# Revit family: Quantum_Odyssey_FBS2LED-DIF-xx_Non-Hosted_R16
name_source: partatom
category: Lighting Fixtures
revit_build: Autodesk Revit 2016 (Build: 20151007_0715(x64)
units: mm (PartAtom-declared; Revit-internal decimal feet)

## family parameters
Always vertical = Yes
Cut with Voids When Loaded = No
Light Source = Yes
OmniClass Number = 23.80.70.00
OmniClass Title = Lighting
Part Type = Normal
Room Calculation Point = No
Round Connector Dimension = Use Diameter
Shared = No
Work Plane-Based = No

## types (3) — shared parameters
Color Filter = 16777215
Construction = Powder Coated Steel Body and PC/ABS End Caps
Diffuser = Acrylic Prismatic Diffuser
Dimensions (L x W x H) = 630mm x 120mm x 108mm
Dimming Lamp Color Temperature Shift = <None>
Emit Shape Visible in Rendering = No
IP Rating = IP20
Lamp = LED Strip Module, 4,000K Natural White, 50,000h Life [L70/B50 Ta 40°C], Ra>80
Manufacturer = Clevertronics
Mounting = Surface mount
Operating Temperature = 1˚C to 40˚C
Operating Voltage = 240V AC; 50Hz
Photometric Web File = ll21966_FBS2LED-DIF_AUB04610050001.ies
Power Factor = 0.95
Replacement lamp = 8002695 PCA:LED Strip 8S6P, ALS-13-840-0-02-B
Tilt Angle = 90.00°
Weight = 1.8 kg

## per-type parameters (varying)
| type | Description | LED Driver | MIC Number | Power Consumption | Replacement Driver | Sensor | Total Lumen Output |
| FBS2LED-DIF-MS | Odyssey Quantum 240V 600mm LED diffused Batten with Microwave Motion Sensor Control (on/off) | Osram 40W, 500-1050mA, 15-50V | AUB04610070001 | 21 Watts | 1330029 LED Driver – 40w 500-1050 mA, 15-50V | 1190117 Sensor: Microwave motion, IP20, MC6025 | 2187 lm @ 104lm/W |
| FBS2LED-DIF | 240V Odyssey Quantum 600mm LED Diffused Batten | Osram 40W, 500-1050mA, 15-50V | AUB04610050001 | 20W | 1330029 LED Driver – 40w 500-1050 mA, 15-50V |  | 2200lm @ 105lm/W |
| FBS2LED-DIF-DD | 240V Odyssey Quantum LED Diffused Batten with DALI driver | LED DALI Driver 25w 350-1050mA, 20-50V, 50,000h | AUB04610060001 | 21 Watts | 1330038 LED Dali Driver – 25w 350-1050 mA, 20-50V |  | 2187lm @ 102lm/W |

note: column(s) folded — value = type name in every type: Model

## geometry (parser evidence)
native form markers: Sweep x3
no freeform markers — native parametric forms only
